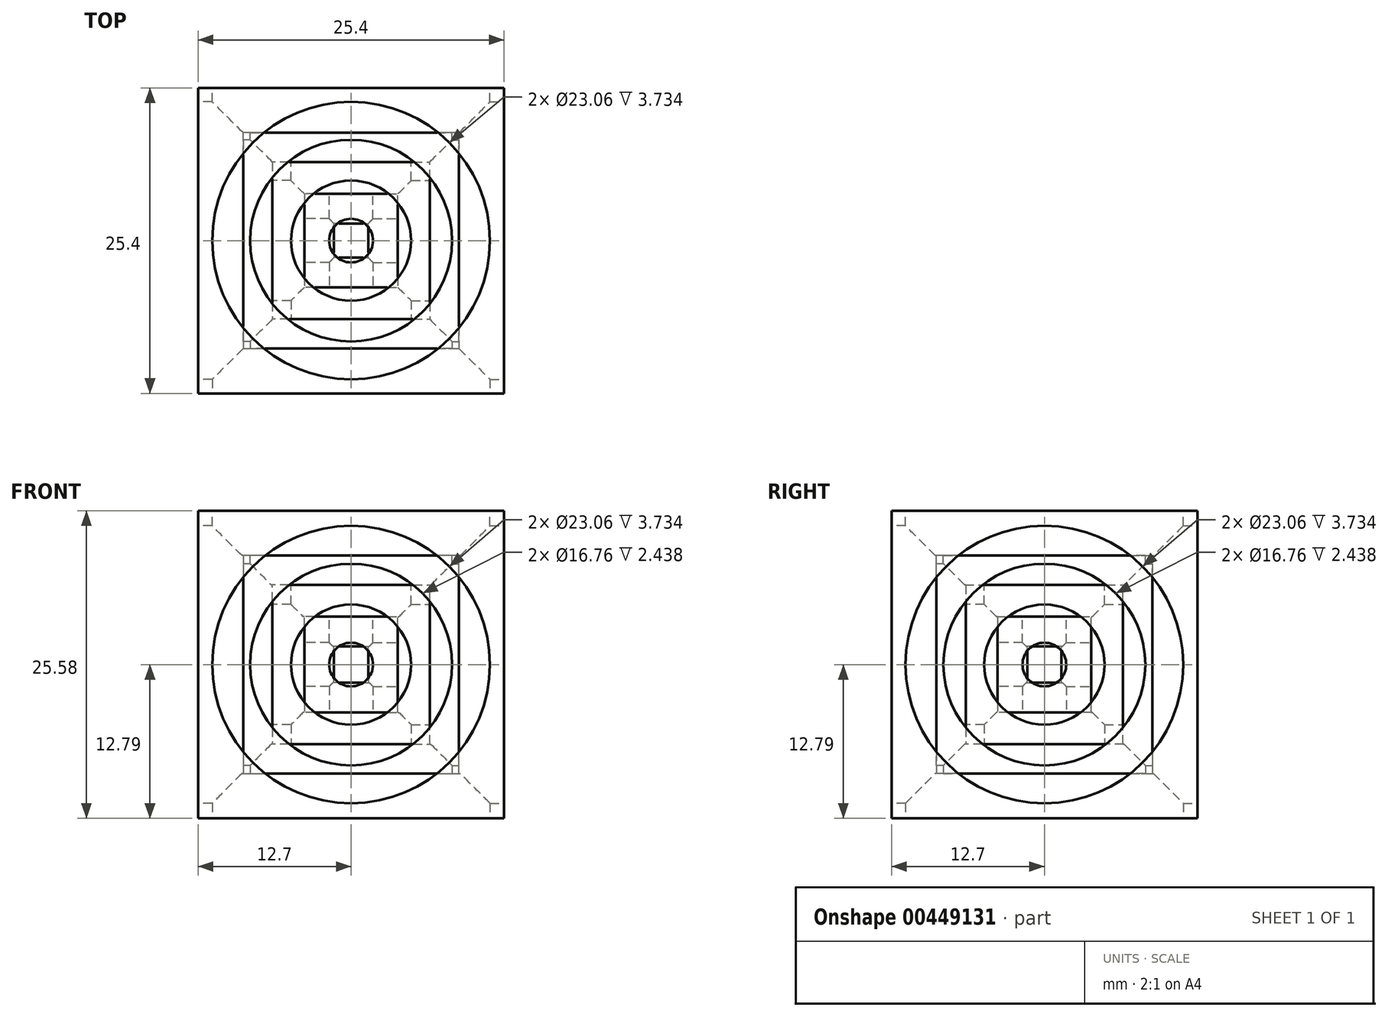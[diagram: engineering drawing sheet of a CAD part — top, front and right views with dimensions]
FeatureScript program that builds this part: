
annotation { "Feature Type Name" : "Feature", "Feature Type Description" : "" }
export const myFeature = defineFeature(function(context is Context, id is Id, definition is map)
    precondition{}
    {
        {
            var Q0;
            Q0=qCreatedBy(makeId("Front.planeOp"),FACE);
            var sketch = newSketch(context, id + "F0", { "sketchPlane" : qUnion([Q0])});
            skLineSegment(sketch, "E0.bottom", {"start": v(12.7, 12.8) * mm, "end": v(-12.7, 12.8) * mm});
            skLineSegment(sketch, "E0.top", {"start": v(12.7, -12.8) * mm, "end": v(-12.7, -12.8) * mm});
            skLineSegment(sketch, "E0.left", {"start": v(12.7, 12.8) * mm, "end": v(12.7, -12.8) * mm});
            skLineSegment(sketch, "E0.right", {"start": v(-12.7, 12.8) * mm, "end": v(-12.7, -12.8) * mm});
            skPoint(sketch, "E0.middle", {"position": v(0, 0) * mm});
            skSolve(sketch);
        }
        {
            var Q0;
            Q0=qCreatedBy(makeId("Front.planeOp"),FACE);
            var sketch = newSketch(context, id + "F1", { "sketchPlane" : qUnion([Q0])});
            skCircle(sketch, "E1", {"center": v(0, 0) * mm, "radius": 11.53 * mm});
            skCircle(sketch, "E2", {"center": v(0, 0) * mm, "radius": 5 * mm});
            skCircle(sketch, "E3", {"center": v(0, 0) * mm, "radius": 8.38 * mm});
            skCircle(sketch, "E4", {"center": v(0, 0) * mm, "radius": 1.82 * mm});
            skSolve(sketch);
        }
        {
            var Q0;
            Q0=qSketchRegion(id+"F0",true);
            extrude(context, id + "F2", {"entities" : qUnion([Q0]), "oppositeDirection" : true, "depth" : 25.4 * mm});
        }
        {
            var Q0;
            Q0=makeQuery(id+"F1.imprint","IMPRINT",FACE,{"disambiguationData":[TD([[makeQuery(id+"F1.imprint","IMPRINT",EDGE,{"derivedFrom":sQuery(id+"F1.wireOp",EDGE,"E4")}),1.0]])]});
            extrude(context, id + "F3", {"entities" : qUnion([Q0]), "operationType" : NewBodyOperationType.REMOVE, "oppositeDirection" : true, "depth" : 11.28 * mm});
        }
        {
            var Q0;
            Q0=makeQuery(id+"F1.imprint","IMPRINT",FACE,{"disambiguationData":[TD([[makeQuery(id+"F1.imprint","IMPRINT",EDGE,{"derivedFrom":sQuery(id+"F1.wireOp",EDGE,"E1")}),1.0]])]});
            var Q1;
            Q1=sQuery(id+"F1.wireOp",EDGE,"E1");
            extrude(context, id + "F4", {"entities" : qUnion([Q0]), "operationType" : NewBodyOperationType.REMOVE, "surfaceEntities" : qUnion([Q1]), "oppositeDirection" : true, "depth" : 3.73 * mm});
        }
        {
            var Q0;
            Q0=makeQuery(id+"F1.imprint","IMPRINT",FACE,{"disambiguationData":[TD([[makeQuery(id+"F1.imprint","IMPRINT",EDGE,{"derivedFrom":sQuery(id+"F1.wireOp",EDGE,"E2")}),1.0]])]});
            var Q1;
            Q1=sQuery(id+"F1.wireOp",EDGE,"E2");
            extrude(context, id + "F5", {"entities" : qUnion([Q0]), "operationType" : NewBodyOperationType.REMOVE, "surfaceEntities" : qUnion([Q1]), "oppositeDirection" : true, "depth" : 8.8 * mm});
        }
        {
            var Q0;
            Q0=makeQuery(id+"F1.imprint","IMPRINT",FACE,{"disambiguationData":[TD([[makeQuery(id+"F1.imprint","IMPRINT",EDGE,{"derivedFrom":sQuery(id+"F1.wireOp",EDGE,"E2")}),-1.0]])]});
            extrude(context, id + "F6", {"entities" : qUnion([Q0]), "operationType" : NewBodyOperationType.REMOVE, "oppositeDirection" : true, "depth" : 6.17 * mm});
        }
        {
            var Q0;
            Q0=makeQuery(id+"F2.opExtrude","SWEPT_FACE",FACE,{"disambiguationData":[OSD([sQuery(id+"F0.wireOp",EDGE,"E0.right")])]});
            var sketch = newSketch(context, id + "F7", { "sketchPlane" : qUnion([Q0])});
            skCircle(sketch, "E5", {"center": v(-12.7, 0) * mm, "radius": 11.53 * mm});
            skCircle(sketch, "E6", {"center": v(-12.7, 0) * mm, "radius": 5 * mm});
            skCircle(sketch, "E7", {"center": v(-12.7, 0) * mm, "radius": 8.38 * mm});
            skCircle(sketch, "E8", {"center": v(-12.7, 0) * mm, "radius": 1.82 * mm});
            skSolve(sketch);
        }
        {
            var Q0;
            Q0=makeQuery(id+"F2.opExtrude","SWEPT_FACE",FACE,{"disambiguationData":[OSD([sQuery(id+"F0.wireOp",EDGE,"E0.top")])]});
            var sketch = newSketch(context, id + "F8", { "sketchPlane" : qUnion([Q0])});
            skCircle(sketch, "E9", {"center": v(0, -12.7) * mm, "radius": 11.53 * mm});
            skCircle(sketch, "E10", {"center": v(0, -12.7) * mm, "radius": 5 * mm});
            skCircle(sketch, "E11", {"center": v(0, -12.7) * mm, "radius": 8.38 * mm});
            skCircle(sketch, "E12", {"center": v(0, -12.7) * mm, "radius": 1.82 * mm});
            skSolve(sketch);
        }
        {
            var Q0;
            Q0=makeQuery(id+"F2.opExtrude","SWEPT_FACE",FACE,{"disambiguationData":[OSD([sQuery(id+"F0.wireOp",EDGE,"E0.bottom")])]});
            var sketch = newSketch(context, id + "F9", { "sketchPlane" : qUnion([Q0])});
            skCircle(sketch, "E13", {"center": v(0, 12.7) * mm, "radius": 11.53 * mm});
            skCircle(sketch, "E14", {"center": v(0, 12.7) * mm, "radius": 5 * mm});
            skCircle(sketch, "E15", {"center": v(0, 12.7) * mm, "radius": 8.38 * mm});
            skCircle(sketch, "E16", {"center": v(0, 12.7) * mm, "radius": 1.82 * mm});
            skSolve(sketch);
        }
        {
            var Q0;
            Q0=makeQuery(id+"F2.opExtrude","SWEPT_FACE",FACE,{"disambiguationData":[OSD([sQuery(id+"F0.wireOp",EDGE,"E0.left")])]});
            var sketch = newSketch(context, id + "F10", { "sketchPlane" : qUnion([Q0])});
            skCircle(sketch, "E17", {"center": v(12.7, 0) * mm, "radius": 11.53 * mm});
            skCircle(sketch, "E18", {"center": v(12.7, 0) * mm, "radius": 5 * mm});
            skCircle(sketch, "E19", {"center": v(12.7, 0) * mm, "radius": 8.38 * mm});
            skCircle(sketch, "E20", {"center": v(12.7, 0) * mm, "radius": 1.82 * mm});
            skSolve(sketch);
        }
        {
            var Q0;
            Q0=makeQuery(id+"F2.opExtrude","CAP_FACE",FACE,{"disambiguationData":[OSD([sQuery(id+"F0.wireOp",EDGE,"E0.bottom"),sQuery(id+"F0.wireOp",EDGE,"E0.top"),sQuery(id+"F0.wireOp",EDGE,"E0.left"),sQuery(id+"F0.wireOp",EDGE,"E0.right")])],"isStart":false});
            var sketch = newSketch(context, id + "F11", { "sketchPlane" : qUnion([Q0])});
            skCircle(sketch, "E21", {"center": v(0, 0) * mm, "radius": 11.53 * mm});
            skCircle(sketch, "E22", {"center": v(0, 0) * mm, "radius": 5 * mm});
            skCircle(sketch, "E23", {"center": v(0, 0) * mm, "radius": 8.38 * mm});
            skCircle(sketch, "E24", {"center": v(0, 0) * mm, "radius": 1.82 * mm});
            skSolve(sketch);
        }
        {
            var Q0;
            Q0=makeQuery(id+"F7.imprint","IMPRINT",FACE,{"disambiguationData":[TD([[makeQuery(id+"F7.imprint","IMPRINT",EDGE,{"derivedFrom":sQuery(id+"F7.wireOp",EDGE,"E8")}),1.0]])]});
            var Q1;
            Q1=sQuery(id+"F7.wireOp",EDGE,"E8");
            extrude(context, id + "F12", {"entities" : qUnion([Q0]), "operationType" : NewBodyOperationType.REMOVE, "surfaceEntities" : qUnion([Q1]), "oppositeDirection" : true, "depth" : 11.28 * mm});
        }
        {
            var Q0;
            Q0=makeQuery(id+"F8.imprint","IMPRINT",FACE,{"disambiguationData":[TD([[makeQuery(id+"F8.imprint","IMPRINT",EDGE,{"derivedFrom":sQuery(id+"F8.wireOp",EDGE,"E12")}),1.0]])]});
            var Q1;
            Q1=sQuery(id+"F8.wireOp",EDGE,"E12");
            extrude(context, id + "F13", {"entities" : qUnion([Q0]), "operationType" : NewBodyOperationType.REMOVE, "surfaceEntities" : qUnion([Q1]), "oppositeDirection" : true, "depth" : 11.28 * mm});
        }
        {
            var Q0;
            Q0=makeQuery(id+"F9.imprint","IMPRINT",FACE,{"disambiguationData":[TD([[makeQuery(id+"F9.imprint","IMPRINT",EDGE,{"derivedFrom":sQuery(id+"F9.wireOp",EDGE,"E16")}),1.0]])]});
            var Q1;
            Q1=sQuery(id+"F9.wireOp",EDGE,"E16");
            extrude(context, id + "F14", {"entities" : qUnion([Q0]), "operationType" : NewBodyOperationType.REMOVE, "surfaceEntities" : qUnion([Q1]), "oppositeDirection" : true, "depth" : 11.28 * mm});
        }
        {
            var Q0;
            Q0=makeQuery(id+"F11.imprint","IMPRINT",FACE,{"disambiguationData":[TD([[makeQuery(id+"F11.imprint","IMPRINT",EDGE,{"derivedFrom":sQuery(id+"F11.wireOp",EDGE,"E24")}),1.0]])]});
            var Q1;
            Q1=sQuery(id+"F11.wireOp",EDGE,"E24");
            extrude(context, id + "F15", {"entities" : qUnion([Q0]), "operationType" : NewBodyOperationType.REMOVE, "surfaceEntities" : qUnion([Q1]), "oppositeDirection" : true, "depth" : 11.28 * mm});
        }
        {
            var Q0;
            Q0=makeQuery(id+"F10.imprint","IMPRINT",FACE,{"disambiguationData":[TD([[makeQuery(id+"F10.imprint","IMPRINT",EDGE,{"derivedFrom":sQuery(id+"F10.wireOp",EDGE,"E20")}),1.0]])]});
            var Q1;
            Q1=sQuery(id+"F10.wireOp",EDGE,"E20");
            extrude(context, id + "F16", {"entities" : qUnion([Q0]), "operationType" : NewBodyOperationType.REMOVE, "surfaceEntities" : qUnion([Q1]), "oppositeDirection" : true, "depth" : 11.28 * mm});
        }
        {
            var Q0;
            Q0=makeQuery(id+"F9.imprint","IMPRINT",FACE,{"disambiguationData":[TD([[makeQuery(id+"F9.imprint","IMPRINT",EDGE,{"derivedFrom":sQuery(id+"F9.wireOp",EDGE,"E14")}),1.0]])]});
            var Q1;
            Q1=sQuery(id+"F9.wireOp",EDGE,"E14");
            extrude(context, id + "F17", {"entities" : qUnion([Q0]), "operationType" : NewBodyOperationType.REMOVE, "surfaceEntities" : qUnion([Q1]), "oppositeDirection" : true, "depth" : 8.8 * mm});
        }
        {
            var Q0;
            Q0=makeQuery(id+"F11.imprint","IMPRINT",FACE,{"disambiguationData":[TD([[makeQuery(id+"F11.imprint","IMPRINT",EDGE,{"derivedFrom":sQuery(id+"F11.wireOp",EDGE,"E22")}),1.0]])]});
            var Q1;
            Q1=sQuery(id+"F11.wireOp",EDGE,"E22");
            extrude(context, id + "F18", {"entities" : qUnion([Q0]), "operationType" : NewBodyOperationType.REMOVE, "surfaceEntities" : qUnion([Q1]), "oppositeDirection" : true, "depth" : 8.8 * mm});
        }
        {
            var Q0;
            Q0=makeQuery(id+"F11.imprint","IMPRINT",FACE,{"disambiguationData":[TD([[makeQuery(id+"F11.imprint","IMPRINT",EDGE,{"derivedFrom":sQuery(id+"F11.wireOp",EDGE,"E22")}),-1.0]])]});
            var Q1;
            Q1=sQuery(id+"F11.wireOp",EDGE,"E23");
            extrude(context, id + "F19", {"entities" : qUnion([Q0]), "operationType" : NewBodyOperationType.REMOVE, "surfaceEntities" : qUnion([Q1]), "oppositeDirection" : true, "depth" : 6.17 * mm});
        }
        {
            var Q0;
            Q0=makeQuery(id+"F11.imprint","IMPRINT",FACE,{"disambiguationData":[TD([[makeQuery(id+"F11.imprint","IMPRINT",EDGE,{"derivedFrom":sQuery(id+"F11.wireOp",EDGE,"E21")}),1.0]])]});
            var Q1;
            Q1=sQuery(id+"F11.wireOp",EDGE,"E21");
            extrude(context, id + "F20", {"entities" : qUnion([Q0]), "operationType" : NewBodyOperationType.REMOVE, "surfaceEntities" : qUnion([Q1]), "oppositeDirection" : true, "depth" : 3.73 * mm});
        }
        {
            var Q0;
            Q0=makeQuery(id+"F9.imprint","IMPRINT",FACE,{"disambiguationData":[TD([[makeQuery(id+"F9.imprint","IMPRINT",EDGE,{"derivedFrom":sQuery(id+"F9.wireOp",EDGE,"E14")}),1.0]])]});
            var Q1;
            Q1=sQuery(id+"F9.wireOp",EDGE,"E14");
            extrude(context, id + "F21", {"entities" : qUnion([Q0]), "operationType" : NewBodyOperationType.REMOVE, "surfaceEntities" : qUnion([Q1]), "oppositeDirection" : true, "depth" : 8.8 * mm});
        }
        {
            var Q0;
            Q0=makeQuery(id+"F9.imprint","IMPRINT",FACE,{"disambiguationData":[TD([[makeQuery(id+"F9.imprint","IMPRINT",EDGE,{"derivedFrom":sQuery(id+"F9.wireOp",EDGE,"E14")}),-1.0]])]});
            var Q1;
            Q1=sQuery(id+"F9.wireOp",EDGE,"E15");
            extrude(context, id + "F22", {"entities" : qUnion([Q0]), "operationType" : NewBodyOperationType.REMOVE, "surfaceEntities" : qUnion([Q1]), "oppositeDirection" : true, "depth" : 6.17 * mm});
        }
        {
            var Q0;
            Q0=makeQuery(id+"F9.imprint","IMPRINT",FACE,{"disambiguationData":[TD([[makeQuery(id+"F9.imprint","IMPRINT",EDGE,{"derivedFrom":sQuery(id+"F9.wireOp",EDGE,"E13")}),1.0]])]});
            var Q1;
            Q1=sQuery(id+"F9.wireOp",EDGE,"E13");
            extrude(context, id + "F23", {"entities" : qUnion([Q0]), "operationType" : NewBodyOperationType.REMOVE, "surfaceEntities" : qUnion([Q1]), "oppositeDirection" : true, "depth" : 3.73 * mm});
        }
        {
            var Q0;
            Q0=makeQuery(id+"F10.imprint","IMPRINT",FACE,{"disambiguationData":[TD([[makeQuery(id+"F10.imprint","IMPRINT",EDGE,{"derivedFrom":sQuery(id+"F10.wireOp",EDGE,"E18")}),1.0]])]});
            var Q1;
            Q1=sQuery(id+"F10.wireOp",EDGE,"E18");
            extrude(context, id + "F24", {"entities" : qUnion([Q0]), "operationType" : NewBodyOperationType.REMOVE, "surfaceEntities" : qUnion([Q1]), "oppositeDirection" : true, "depth" : 8.8 * mm});
        }
        {
            var Q0;
            Q0=makeQuery(id+"F10.imprint","IMPRINT",FACE,{"disambiguationData":[TD([[makeQuery(id+"F10.imprint","IMPRINT",EDGE,{"derivedFrom":sQuery(id+"F10.wireOp",EDGE,"E18")}),-1.0]])]});
            var Q1;
            Q1=sQuery(id+"F10.wireOp",EDGE,"E19");
            extrude(context, id + "F25", {"entities" : qUnion([Q0]), "operationType" : NewBodyOperationType.REMOVE, "surfaceEntities" : qUnion([Q1]), "oppositeDirection" : true, "depth" : 6.17 * mm});
        }
        {
            var Q0;
            Q0=makeQuery(id+"F10.imprint","IMPRINT",FACE,{"disambiguationData":[TD([[makeQuery(id+"F10.imprint","IMPRINT",EDGE,{"derivedFrom":sQuery(id+"F10.wireOp",EDGE,"E17")}),1.0]])]});
            var Q1;
            Q1=sQuery(id+"F10.wireOp",EDGE,"E17");
            extrude(context, id + "F26", {"entities" : qUnion([Q0]), "operationType" : NewBodyOperationType.REMOVE, "surfaceEntities" : qUnion([Q1]), "oppositeDirection" : true, "depth" : 3.73 * mm});
        }
        {
            var Q0;
            Q0=makeQuery(id+"F8.imprint","IMPRINT",FACE,{"disambiguationData":[TD([[makeQuery(id+"F8.imprint","IMPRINT",EDGE,{"derivedFrom":sQuery(id+"F8.wireOp",EDGE,"E10")}),1.0]])]});
            var Q1;
            Q1=sQuery(id+"F8.wireOp",EDGE,"E10");
            var Q2;
            Q2=sQuery(id+"F9.wireOp",EDGE,"E15");
            var Q3;
            Q3=sQuery(id+"F8.wireOp",EDGE,"E11");
            extrude(context, id + "F27", {"entities" : qUnion([Q0]), "operationType" : NewBodyOperationType.REMOVE, "surfaceEntities" : qUnion([Q1, Q2, Q3]), "oppositeDirection" : true, "depth" : 8.8 * mm});
        }
        {
            var Q0;
            Q0=makeQuery(id+"F8.imprint","IMPRINT",FACE,{"disambiguationData":[TD([[makeQuery(id+"F8.imprint","IMPRINT",EDGE,{"derivedFrom":sQuery(id+"F8.wireOp",EDGE,"E10")}),-1.0]])]});
            var Q1;
            Q1=sQuery(id+"F8.wireOp",EDGE,"E11");
            extrude(context, id + "F28", {"entities" : qUnion([Q0]), "operationType" : NewBodyOperationType.REMOVE, "surfaceEntities" : qUnion([Q1]), "oppositeDirection" : true, "depth" : 6.17 * mm});
        }
        {
            var Q0;
            Q0=makeQuery(id+"F7.imprint","IMPRINT",FACE,{"disambiguationData":[TD([[makeQuery(id+"F7.imprint","IMPRINT",EDGE,{"derivedFrom":sQuery(id+"F7.wireOp",EDGE,"E6")}),1.0]])]});
            var Q1;
            Q1=sQuery(id+"F7.wireOp",EDGE,"E6");
            extrude(context, id + "F29", {"entities" : qUnion([Q0]), "operationType" : NewBodyOperationType.REMOVE, "surfaceEntities" : qUnion([Q1]), "oppositeDirection" : true, "depth" : 8.8 * mm});
        }
        {
            var Q0;
            Q0=makeQuery(id+"F7.imprint","IMPRINT",FACE,{"disambiguationData":[TD([[makeQuery(id+"F7.imprint","IMPRINT",EDGE,{"derivedFrom":sQuery(id+"F7.wireOp",EDGE,"E6")}),-1.0]])]});
            var Q1;
            Q1=sQuery(id+"F7.wireOp",EDGE,"E7");
            extrude(context, id + "F30", {"entities" : qUnion([Q0]), "operationType" : NewBodyOperationType.REMOVE, "surfaceEntities" : qUnion([Q1]), "oppositeDirection" : true, "depth" : 6.17 * mm});
        }
        {
            var Q0;
            Q0=makeQuery(id+"F7.imprint","IMPRINT",FACE,{"disambiguationData":[TD([[makeQuery(id+"F7.imprint","IMPRINT",EDGE,{"derivedFrom":sQuery(id+"F7.wireOp",EDGE,"E5")}),1.0]])]});
            var Q1;
            Q1=sQuery(id+"F7.wireOp",EDGE,"E5");
            extrude(context, id + "F31", {"entities" : qUnion([Q0]), "operationType" : NewBodyOperationType.REMOVE, "surfaceEntities" : qUnion([Q1]), "oppositeDirection" : true, "depth" : 3.73 * mm});
        }
        {
            var Q0;
            Q0=makeQuery(id+"F8.imprint","IMPRINT",FACE,{"disambiguationData":[TD([[makeQuery(id+"F8.imprint","IMPRINT",EDGE,{"derivedFrom":sQuery(id+"F8.wireOp",EDGE,"E9")}),1.0]])]});
            var Q1;
            Q1=sQuery(id+"F8.wireOp",EDGE,"E9");
            extrude(context, id + "F32", {"entities" : qUnion([Q0]), "operationType" : NewBodyOperationType.REMOVE, "surfaceEntities" : qUnion([Q1]), "oppositeDirection" : true, "depth" : 3.73 * mm});
        }
    });
